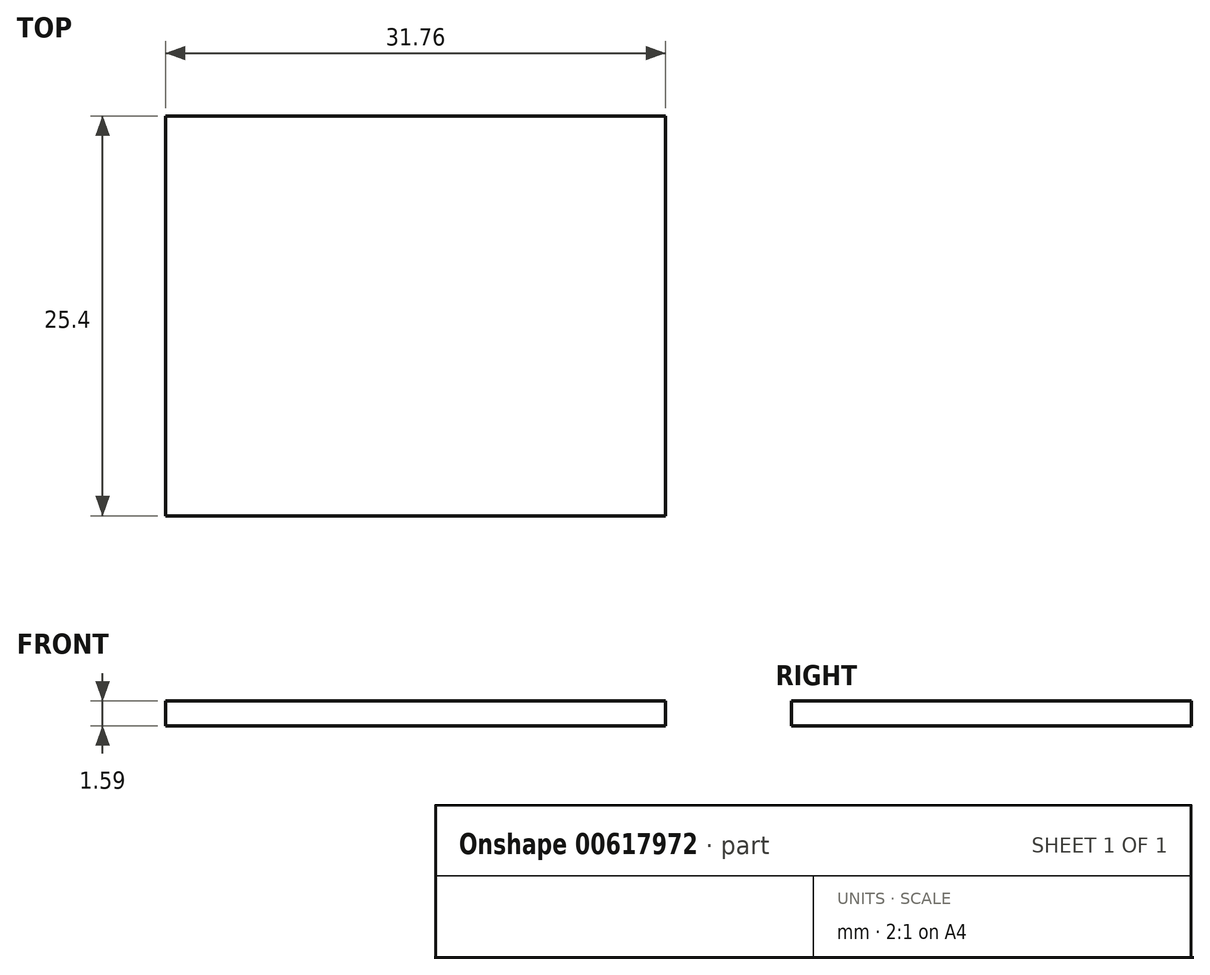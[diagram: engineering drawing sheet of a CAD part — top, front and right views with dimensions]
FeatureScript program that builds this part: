
annotation { "Feature Type Name" : "Feature", "Feature Type Description" : "" }
export const myFeature = defineFeature(function(context is Context, id is Id, definition is map)
    precondition{}
    {
        {
            var Q0;
            Q0=qCreatedBy(makeId("Top.planeOp"),FACE);
            var sketch = newSketch(context, id + "F0", { "sketchPlane" : qUnion([Q0])});
            skLineSegment(sketch, "E0.bottom", {"start": v(-15.88, 12.7) * mm, "end": v(15.88, 12.7) * mm});
            skLineSegment(sketch, "E0.top", {"start": v(-15.88, -12.7) * mm, "end": v(15.88, -12.7) * mm});
            skLineSegment(sketch, "E0.left", {"start": v(-15.88, 12.7) * mm, "end": v(-15.88, -12.7) * mm});
            skLineSegment(sketch, "E0.right", {"start": v(15.88, 12.7) * mm, "end": v(15.88, -12.7) * mm});
            skPoint(sketch, "E0.middle", {"position": v(0, 0) * mm});
            skSolve(sketch);
        }
        {
            var Q0;
            Q0=makeQuery(id+"F0.imprint","IMPRINT",FACE,{"disambiguationData":[TD([[makeQuery(id+"F0.imprint","IMPRINT",EDGE,{"derivedFrom":sQuery(id+"F0.wireOp",EDGE,"E0.bottom")}),-1.0]])]});
            extrude(context, id + "F1", {"entities" : qUnion([Q0]), "depth" : 1.59 * mm, "offsetDistance" : 25 * mm});
        }
    });
